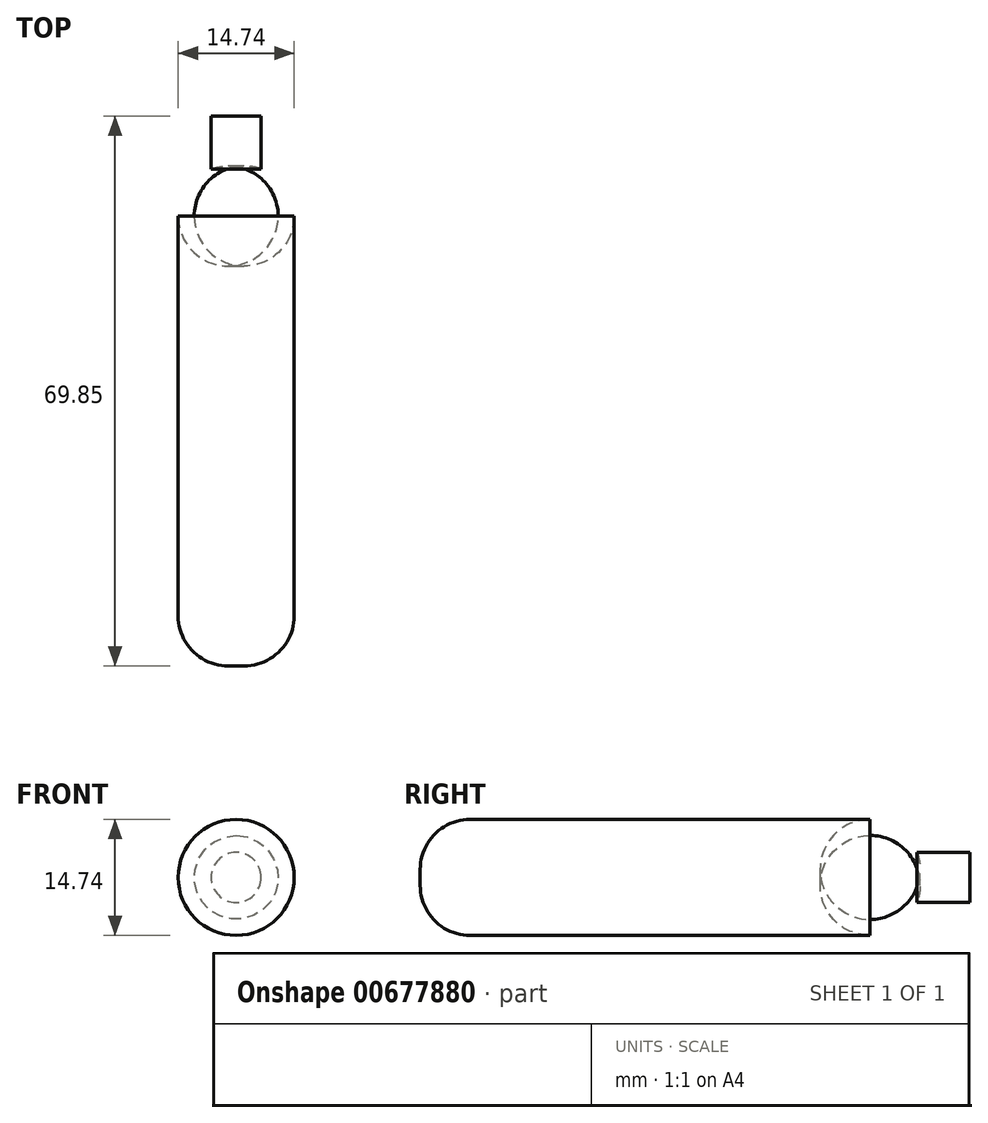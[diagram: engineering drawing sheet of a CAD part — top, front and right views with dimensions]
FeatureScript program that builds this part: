
annotation { "Feature Type Name" : "Feature", "Feature Type Description" : "" }
export const myFeature = defineFeature(function(context is Context, id is Id, definition is map)
    precondition{}
    {
        {
            var Q0;
            Q0=qCreatedBy(makeId("Front.planeOp"),FACE);
            var sketch = newSketch(context, id + "F0", { "sketchPlane" : qUnion([Q0])});
            skCircle(sketch, "E0", {"center": v(0, 0) * mm, "radius": 7.37 * mm});
            skSolve(sketch);
        }
        {
            var Q0;
            Q0=makeQuery(id+"F0.imprint","IMPRINT",FACE,{"disambiguationData":[TD([[makeQuery(id+"F0.imprint","IMPRINT",EDGE,{"derivedFrom":sQuery(id+"F0.wireOp",EDGE,"E0")}),1.0]])]});
            extrude(context, id + "F1", {"entities" : qUnion([Q0]), "depth" : 63.5 * mm, "offsetDistance" : 25.4 * mm});
        }
        {
            var Q0;
            Q0=makeQuery(id+"F1.opExtrude","CAP_FACE",FACE,{"disambiguationData":[OSD([sQuery(id+"F0.wireOp",EDGE,"E0")])],"isStart":false});
            fillet(context, id + "F2", {"entities" : qUnion([Q0]), "radius" : 6.35 * mm, "tangentPropagation" : true, "allowEdgeOverflow" : false});
        }
        {
            var Q0;
            Q0=makeQuery(id+"F1.opExtrude","CAP_FACE",FACE,{"disambiguationData":[OSD([sQuery(id+"F0.wireOp",EDGE,"E0")])],"isStart":true});
            fillet(context, id + "F3", {"entities" : qUnion([Q0]), "radius" : 6.35 * mm, "tangentPropagation" : true, "allowEdgeOverflow" : false});
        }
        {
            var Q0;
            Q0=qCreatedBy(makeId("Front.planeOp"),FACE);
            var sketch = newSketch(context, id + "F4", { "sketchPlane" : qUnion([Q0])});
            skCircle(sketch, "E1", {"center": v(0, 0) * mm, "radius": 3.18 * mm});
            skSolve(sketch);
        }
        {
            var Q0;
            Q0 = qSketchRegion(id + "F4", true);
            extrude(context, id + "F5", {"entities" : qUnion([Q0]), "operationType" : NewBodyOperationType.ADD, "endBound" : BoundingType.SYMMETRIC, "depth" : 12.7 * mm, "offsetDistance" : 25.4 * mm});
        }
    });
